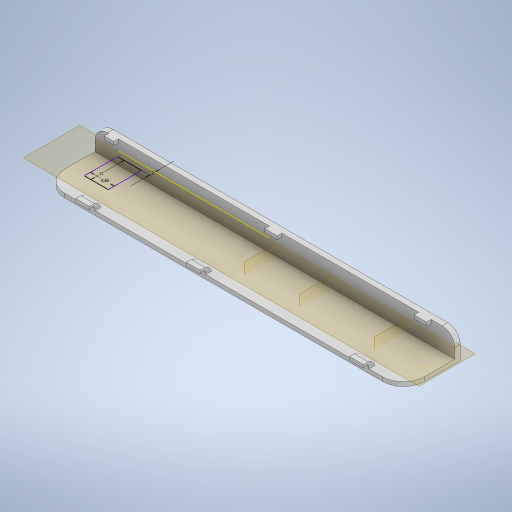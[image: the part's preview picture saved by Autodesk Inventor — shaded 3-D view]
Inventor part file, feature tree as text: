
AUTODESK INVENTOR PART (.ipt)
format: ipt  version: 2024.2 (Build 282272000, 272)  size: 363,008 bytes
history: native  units: mm
features: sketch x6, other x5, extrude x4, fillet x2, mirror x2
ambient origin geometry x8: Origin, YZ Plane, XZ Plane, XY Plane, X Axis, Y Axis, Z Axis, Center Point
bodies: Body1 (feature_tree)
feature tree (19):
  other  "Твердое тело1"
  extrude  "Выдавливание1"  Depth=20.5mm
  extrude  "Выдавливание2"  Depth=130.0mm
  fillet  "Сопряжение1"  Radius=7.5mm
  fillet  "Сопряжение2"  Radius=7.5mm
  extrude  "Выдавливание3"  Depth=1.5mm TaperAngle=0.0deg
  other  "РабПлоскость1"
  extrude  "Выдавливание4"  Depth=2.0mm
  other  "РабПлоскость2"
  mirror  "Зеркальное отражение1"
  other  "РабПлоскость3"
  mirror  "Зеркальное отражение2"
  sketch  "Эскиз5"
  other  "РабПлоскость4"
  sketch  "Эскиз6"
  sketch  "Эскиз1"
  sketch  "Эскиз2"
  sketch  "Эскиз3"
  sketch  "Эскиз4"
